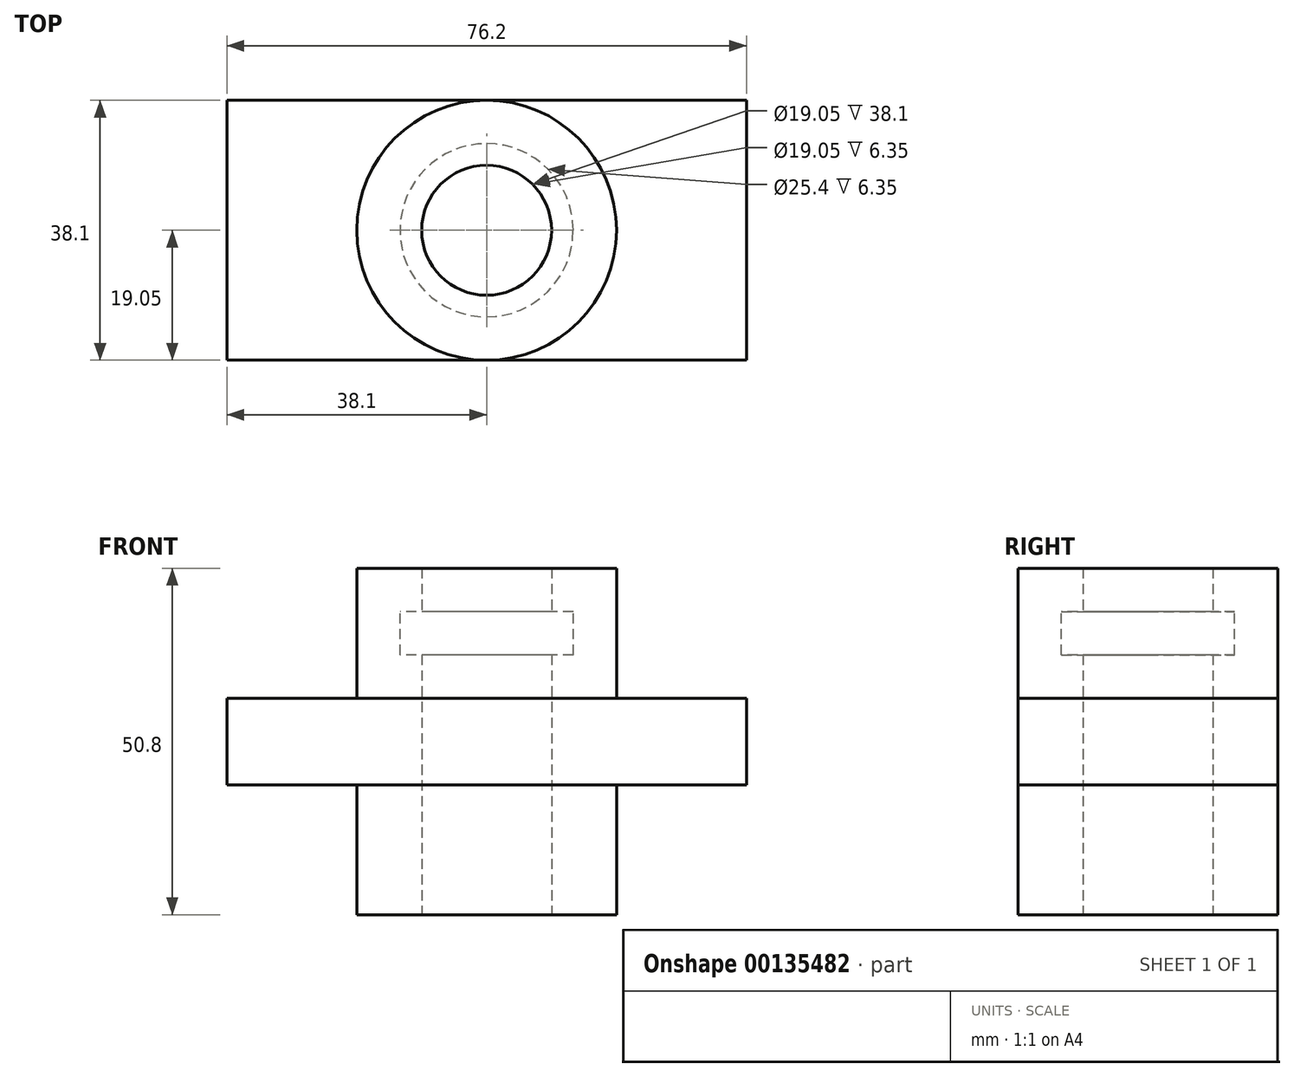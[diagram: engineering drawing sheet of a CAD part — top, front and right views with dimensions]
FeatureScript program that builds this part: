
annotation { "Feature Type Name" : "Feature", "Feature Type Description" : "" }
export const myFeature = defineFeature(function(context is Context, id is Id, definition is map)
    precondition{}
    {
        {
            var Q0;
            Q0=qCreatedBy(makeId("Top.planeOp"),FACE);
            var sketch = newSketch(context, id + "F0", { "sketchPlane" : qUnion([Q0])});
            skLineSegment(sketch, "E0.bottom", {"start": v(0, 0) * mm, "end": v(76.2, 0) * mm});
            skLineSegment(sketch, "E0.top", {"start": v(0, 38.1) * mm, "end": v(76.2, 38.1) * mm});
            skLineSegment(sketch, "E0.left", {"start": v(0, 0) * mm, "end": v(0, 38.1) * mm});
            skLineSegment(sketch, "E0.right", {"start": v(76.2, 0) * mm, "end": v(76.2, 38.1) * mm});
            skCircle(sketch, "E1", {"center": v(38.1, 19.05) * mm, "radius": 19.05 * mm});
            skPoint(sketch, "E1.centerSnap0", {"position": v(76.2, 19.05) * mm});
            skPoint(sketch, "E1.centerSnap1", {"position": v(38.1, 38.1) * mm});
            skCircle(sketch, "E2", {"center": v(38.1, 19.05) * mm, "radius": 9.53 * mm});
            skSolve(sketch);
        }
        {
            var Q0;
            Q0=makeQuery(id+"F0.imprint","IMPRINT",FACE,{"disambiguationData":[TD([[makeQuery(id+"F0.imprint","IMPRINT",EDGE,{"derivedFrom":sQuery(id+"F0.wireOp",EDGE,"E2")}),-1.0]])]});
            extrude(context, id + "F1", {"entities" : qUnion([Q0]), "endBound" : BoundingType.SYMMETRIC, "depth" : 50.8 * mm});
        }
        {
            var Q0;
            {var subQ0=sQuery(id+"F0.wireOp",EDGE,"E0.right");Q0=makeQuery(id+"F0.imprint","IMPRINT",FACE,{"disambiguationData":[TD([[makeQuery(id+"F0.imprint","IMPRINT",EDGE,{"derivedFrom":subQ0}),1.0]])]});}
            var Q1;
            {var subQ0=sQuery(id+"F0.wireOp",EDGE,"E0.left");Q1=makeQuery(id+"F0.imprint","IMPRINT",FACE,{"disambiguationData":[TD([[makeQuery(id+"F0.imprint","IMPRINT",EDGE,{"derivedFrom":subQ0}),-1.0]])]});}
            extrude(context, id + "F2", {"entities" : qUnion([Q0, Q1]), "operationType" : NewBodyOperationType.ADD, "endBound" : BoundingType.SYMMETRIC, "depth" : 12.7 * mm});
        }
        {
            var Q0;
            Q0=makeQuery(id+"F1.opExtrude","CAP_FACE",FACE,{"disambiguationData":[OSD([sQuery(id+"F0.wireOp",EDGE,"E1"),sQuery(id+"F0.wireOp",EDGE,"E2")])],"isStart":false});
            var sketch = newSketch(context, id + "F3", { "sketchPlane" : qUnion([Q0])});
            skCircle(sketch, "E3", {"center": v(38.1, 19.05) * mm, "radius": 12.7 * mm});
            skCircle(sketch, "E4", {"center": v(38.1, 19.05) * mm, "radius": 9.53 * mm});
            skCircle(sketch, "E5", {"center": v(38.1, 19.05) * mm, "radius": 19.05 * mm});
            skSolve(sketch);
        }
        {
            var Q0;
            Q0=makeQuery(id+"F3.imprint","IMPRINT",FACE,{"disambiguationData":[TD([[makeQuery(id+"F3.imprint","IMPRINT",EDGE,{"derivedFrom":sQuery(id+"F3.wireOp",EDGE,"E3")}),1.0]])]});
            extrude(context, id + "F4", {"entities" : qUnion([Q0]), "operationType" : NewBodyOperationType.REMOVE, "oppositeDirection" : true, "depth" : 12.7 * mm, "hasSecondDirection" : true, "secondDirectionOppositeDirection" : true, "secondDirectionDepth" : 6.35 * mm});
        }
    });
